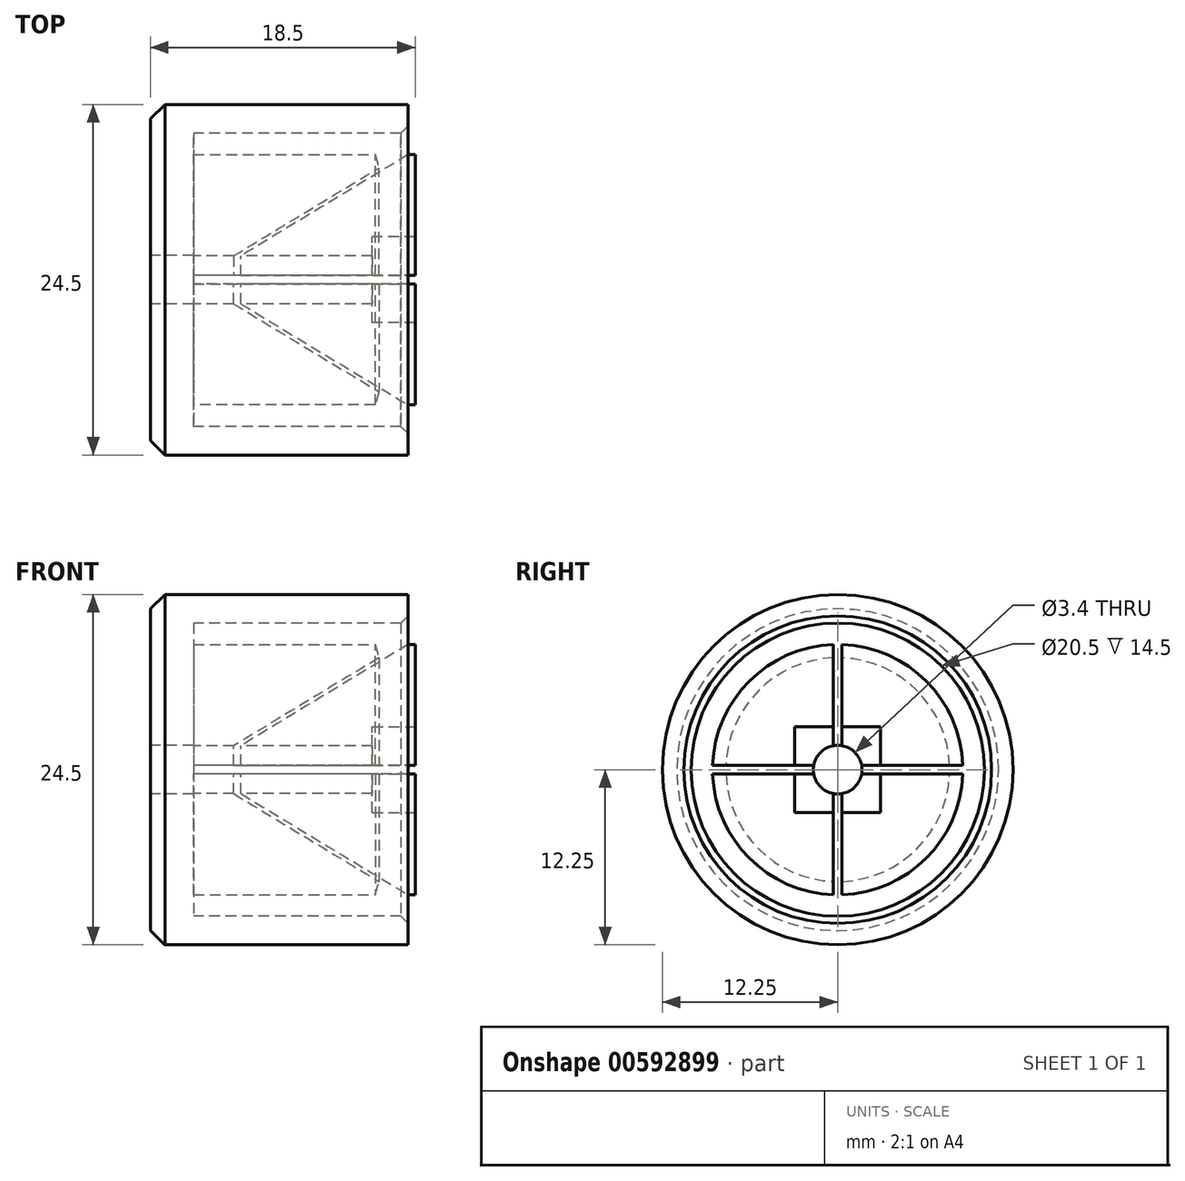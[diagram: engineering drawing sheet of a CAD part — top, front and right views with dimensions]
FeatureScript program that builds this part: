
annotation { "Feature Type Name" : "Feature", "Feature Type Description" : "" }
export const myFeature = defineFeature(function(context is Context, id is Id, definition is map)
    precondition{}
    {
        {
            assignVariable(context, id + "F0", {"name" : "NutDepth", "anyValue" : 3});
        }
        {
            var Q0;
            Q0=qCreatedBy(makeId("Front.planeOp"),FACE);
            var sketch = newSketch(context, id + "F1", { "sketchPlane" : qUnion([Q0])});
            skLineSegment(sketch, "E0", {"start": v(0, 12.25) * mm, "end": v(0, 0) * mm});
            skLineSegment(sketch, "E1", {"start": v(18, 0) * mm, "end": v(18, 8.75) * mm});
            skLineSegment(sketch, "E2", {"start": v(18, 8.75) * mm, "end": v(3, 8.75) * mm});
            skLineSegment(sketch, "E3", {"start": v(3, 8.75) * mm, "end": v(3, 10.25) * mm});
            skLineSegment(sketch, "E4", {"start": v(3, 10.25) * mm, "end": v(18, 10.25) * mm});
            skLineSegment(sketch, "E5", {"start": v(18, 10.25) * mm, "end": v(18, 12.25) * mm});
            skLineSegment(sketch, "E6", {"start": v(18, 12.25) * mm, "end": v(0, 12.25) * mm});
            skLineSegment(sketch, "E7", {"start": v(0, 0) * mm, "end": v(18, 0) * mm});
            skLineSegment(sketch, "E8", {"start": v(3, 8.75) * mm, "end": v(3, 0) * mm, "construction": true});
            skLineSegment(sketch, "E9", {"start": v(0, 1.7) * mm, "end": v(18, 1.7) * mm});
            skLineSegment(sketch, "E10", {"start": v(17.5, 8.75) * mm, "end": v(3, 0) * mm});
            skPoint(sketch, "E11", {"position": v(17.5, 8.75) * mm});
            skSolve(sketch);
        }
        {
            var Q0;
            {var subQ0=sQuery(id+"F1.wireOp",EDGE,"E3");Q0=makeQuery(id+"F1.imprint","IMPRINT",FACE,{"disambiguationData":[TD([[makeQuery(id+"F1.imprint","IMPRINT",EDGE,{"derivedFrom":subQ0}),1.0]])]});}
            var Q1;
            Q1=sQuery(id+"F1.wireOp",EDGE,"E7");
            revolve(context, id + "F2", {"entities" : qUnion([Q0]), "axis" : qUnion([Q1]), "revolveType" : RevolveType.FULL});
        }
        {
            var Q0;
            {var subQ1=sQuery(id+"F1.wireOp",EDGE,"E1");var subQ3=sQuery(id+"F1.wireOp",EDGE,"E9");var subQ4=makeQuery(id+"F1.imprint","INTERSECT",VERTEX,{"derivedFrom":[subQ1,subQ3]});Q0=makeQuery(id+"F1.imprint","IMPRINT",FACE,{"disambiguationData":[TD([[makeQuery(id+"F1.imprint","IMPRINT",EDGE,{"disambiguationData":[TD([[subQ4,1.0]])],"derivedFrom":subQ3}),1.0]])]});}
            var Q1;
            Q1=sQuery(id+"F1.wireOp",EDGE,"E7");
            revolve(context, id + "F3", {"entities" : qUnion([Q0]), "axis" : qUnion([Q1]), "revolveType" : RevolveType.FULL});
        }
        {
            var Q0;
            Q0=makeQuery(id+"F2.opRevolve","SWEPT_FACE",FACE,{"disambiguationData":[OSD([sQuery(id+"F1.wireOp",EDGE,"E5")])]});
            var sketch = newSketch(context, id + "F4", { "sketchPlane" : qUnion([Q0])});
            skLineSegment(sketch, "E12", {"start": v(-0.3, 8.75) * mm, "end": v(-0.3, 0.3) * mm});
            skLineSegment(sketch, "E13", {"start": v(-0.3, 0.3) * mm, "end": v(-8.75, 0.3) * mm});
            skLineSegment(sketch, "E14", {"start": v(-8.75, 0.3) * mm, "end": v(-8.75, -0.3) * mm});
            skLineSegment(sketch, "E15", {"start": v(-8.75, -0.3) * mm, "end": v(-0.3, -0.3) * mm});
            skLineSegment(sketch, "E16", {"start": v(-0.3, -0.3) * mm, "end": v(-0.3, -8.75) * mm});
            skLineSegment(sketch, "E17", {"start": v(-0.3, -8.75) * mm, "end": v(0.3, -8.75) * mm});
            skLineSegment(sketch, "E18", {"start": v(0.3, -8.75) * mm, "end": v(0.3, -0.3) * mm});
            skLineSegment(sketch, "E19", {"start": v(0.3, -0.3) * mm, "end": v(8.75, -0.3) * mm});
            skLineSegment(sketch, "E20", {"start": v(8.75, -0.3) * mm, "end": v(8.75, 0.3) * mm});
            skLineSegment(sketch, "E21", {"start": v(8.75, 0.3) * mm, "end": v(0.3, 0.3) * mm});
            skLineSegment(sketch, "E22", {"start": v(0.3, 0.3) * mm, "end": v(0.3, 8.75) * mm});
            skLineSegment(sketch, "E23", {"start": v(0.3, 8.75) * mm, "end": v(-0.3, 8.75) * mm});
            skLineSegment(sketch, "E24", {"start": v(-0.3, -0.3) * mm, "end": v(0.3, 0.3) * mm, "construction": true});
            skPoint(sketch, "E25", {"position": v(0, 8.75) * mm});
            skSolve(sketch);
        }
        {
            var Q0;
            Q0 = qSketchRegion(id + "F4", true);
            var Q1;
            Q1=makeQuery(id+"F2.opRevolve","SWEPT_FACE",FACE,{"disambiguationData":[OSD([sQuery(id+"F1.wireOp",EDGE,"E3")])]});
            extrude(context, id + "F5", {"entities" : qUnion([Q0]), "operationType" : NewBodyOperationType.REMOVE, "endBound" : BoundingType.UP_TO_SURFACE, "oppositeDirection" : true, "depth" : 25 * mm, "endBoundEntityFace" : qUnion([Q1]), "offsetDistance" : 25 * mm});
        }
        {
            var Q0;
            {var subQ0=sQuery(id+"F1.wireOp",EDGE,"E2");var subQ1=sQuery(id+"F1.wireOp",EDGE,"E10");Q0=makeQuery(id+"F5.boolean.opBoolean","SPLIT",EDGE,{"disambiguationData":[TD([makeQuery(id+"F5.opExtrude","SWEPT_FACE",FACE,{"disambiguationData":[OSD([sQuery(id+"F4.wireOp",EDGE,"E21")])]})])],"derivedFrom":makeQuery(id+"F2.opRevolve","SWEPT_EDGE",EDGE,{"disambiguationData":[OSD([sQuery(id+"F1.wireOp",EDGE,"E1"),subQ0,subQ1])]})});}
            var Q1;
            {var subQ0=sQuery(id+"F1.wireOp",EDGE,"E2");var subQ1=sQuery(id+"F1.wireOp",EDGE,"E10");Q1=makeQuery(id+"F5.boolean.opBoolean","SPLIT",EDGE,{"disambiguationData":[TD([makeQuery(id+"F5.opExtrude","SWEPT_FACE",FACE,{"disambiguationData":[OSD([sQuery(id+"F4.wireOp",EDGE,"E18")])]})])],"derivedFrom":makeQuery(id+"F2.opRevolve","SWEPT_EDGE",EDGE,{"disambiguationData":[OSD([sQuery(id+"F1.wireOp",EDGE,"E1"),subQ0,subQ1])]})});}
            var Q2;
            {var subQ0=sQuery(id+"F1.wireOp",EDGE,"E2");var subQ1=sQuery(id+"F1.wireOp",EDGE,"E10");Q2=makeQuery(id+"F5.boolean.opBoolean","SPLIT",EDGE,{"disambiguationData":[TD([makeQuery(id+"F5.opExtrude","SWEPT_FACE",FACE,{"disambiguationData":[OSD([sQuery(id+"F4.wireOp",EDGE,"E15")])]})])],"derivedFrom":makeQuery(id+"F2.opRevolve","SWEPT_EDGE",EDGE,{"disambiguationData":[OSD([sQuery(id+"F1.wireOp",EDGE,"E1"),subQ0,subQ1])]})});}
            var Q3;
            {var subQ0=sQuery(id+"F1.wireOp",EDGE,"E2");var subQ1=sQuery(id+"F1.wireOp",EDGE,"E10");Q3=makeQuery(id+"F5.boolean.opBoolean","SPLIT",EDGE,{"disambiguationData":[TD([makeQuery(id+"F5.opExtrude","SWEPT_FACE",FACE,{"disambiguationData":[OSD([sQuery(id+"F4.wireOp",EDGE,"E12")])]})])],"derivedFrom":makeQuery(id+"F2.opRevolve","SWEPT_EDGE",EDGE,{"disambiguationData":[OSD([sQuery(id+"F1.wireOp",EDGE,"E1"),subQ0,subQ1])]})});}
            chamfer(context, id + "F6", {"entities" : qUnion([Q0, Q1, Q2, Q3]), "width" : 0.5 * mm, "tangentPropagation" : true});
        }
        {
            var Q0;
            Q0=makeQuery(id+"F2.opRevolve","SWEPT_EDGE",EDGE,{"disambiguationData":[OSD([sQuery(id+"F1.wireOp",EDGE,"E4"),sQuery(id+"F1.wireOp",EDGE,"E5")])]});
            chamfer(context, id + "F7", {"entities" : qUnion([Q0]), "width" : 0.5 * mm, "tangentPropagation" : true});
        }
        {
            var Q0;
            Q0=makeQuery(id+"F2.opRevolve","SWEPT_EDGE",EDGE,{"disambiguationData":[OSD([sQuery(id+"F1.wireOp",EDGE,"E0"),sQuery(id+"F1.wireOp",EDGE,"E6")])]});
            chamfer(context, id + "F8", {"entities" : qUnion([Q0]), "width" : 1 * mm, "tangentPropagation" : true});
        }
        {
            var Q0;
            Q0=makeQuery(id+"F3.opRevolve","SWEPT_BODY",BODY,{"disambiguationData":[OSD([sQuery(id+"F1.wireOp",EDGE,"E1"),sQuery(id+"F1.wireOp",EDGE,"E9"),sQuery(id+"F1.wireOp",EDGE,"E10")])]});
            transform(context, id + "F9", {"entities" : qUnion([Q0]), "transformType" : TransformType.TRANSLATION_3D, "dx" : 0.5 * mm, "dy" : 0 * mm, "dz" : 0 * mm, "makeCopy" : false});
        }
        {
            var Q0;
            Q0=makeQuery(id+"F3.opRevolve","SWEPT_FACE",FACE,{"disambiguationData":[OSD([sQuery(id+"F1.wireOp",EDGE,"E1")])]});
            var sketch = newSketch(context, id + "F10", { "sketchPlane" : qUnion([Q0])});
            skLineSegment(sketch, "E26.bottom", {"start": v(-3, -3) * mm, "end": v(3, -3) * mm});
            skLineSegment(sketch, "E26.top", {"start": v(-3, 3) * mm, "end": v(3, 3) * mm});
            skLineSegment(sketch, "E26.left", {"start": v(-3, -3) * mm, "end": v(-3, 3) * mm});
            skLineSegment(sketch, "E26.right", {"start": v(3, -3) * mm, "end": v(3, 3) * mm});
            skPoint(sketch, "E26.middle", {"position": v(0, 0) * mm});
            skSolve(sketch);
        }
        {
            var Q0;
            Q0 = qSketchRegion(id + "F10", true);
            extrude(context, id + "F11", {"entities" : qUnion([Q0]), "operationType" : NewBodyOperationType.REMOVE, "oppositeDirection" : true, "depth" : (getVariable(context, 'NutDepth')) * mm, "offsetDistance" : 25 * mm});
        }
    });
